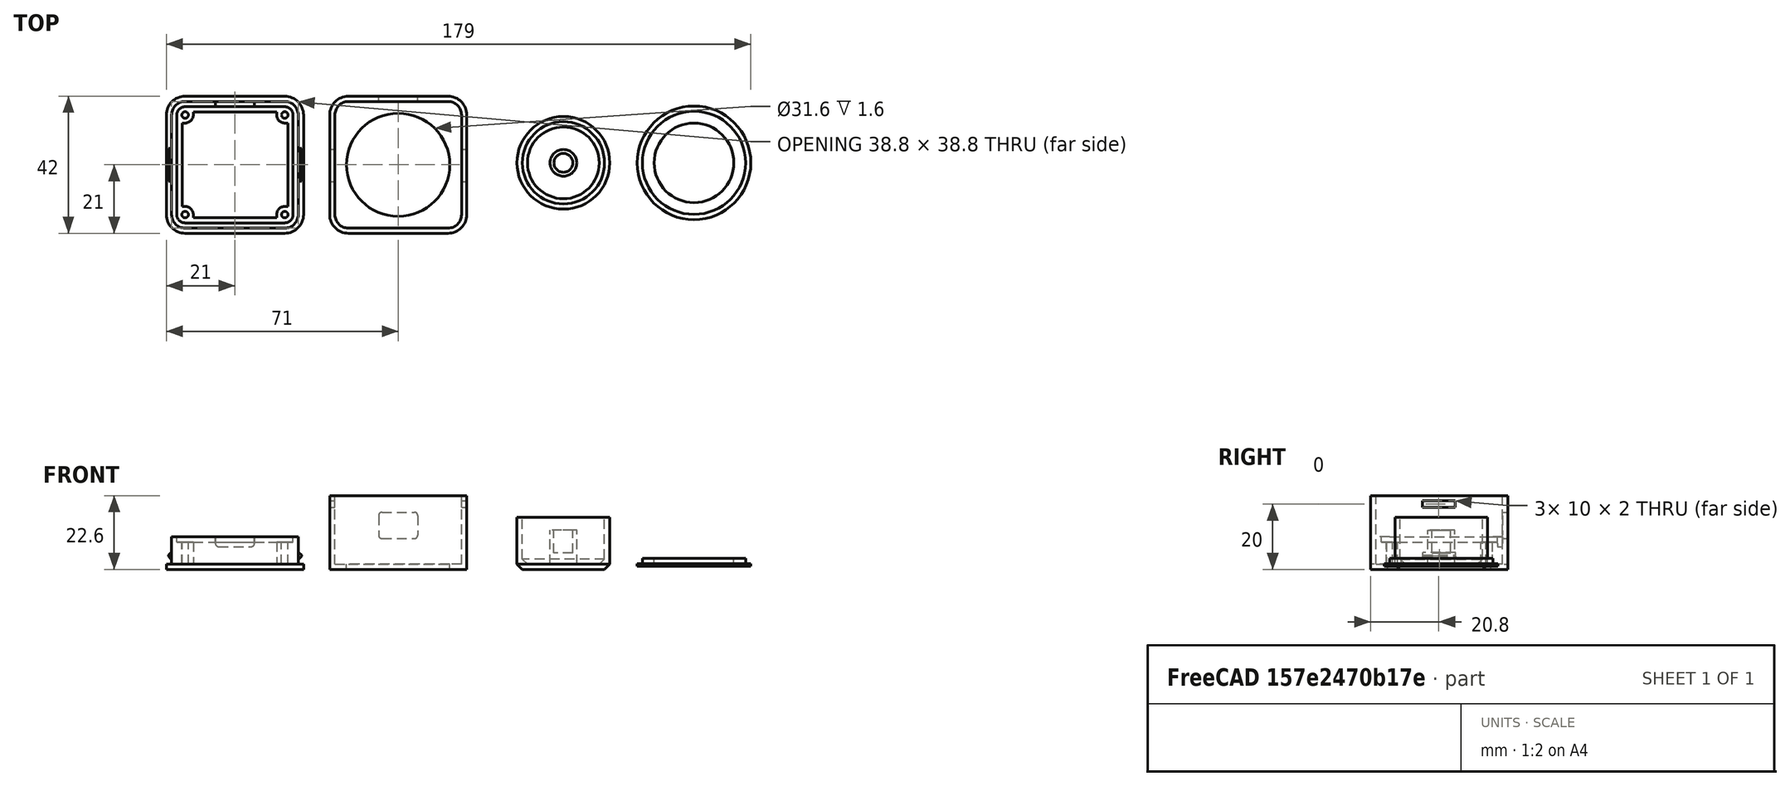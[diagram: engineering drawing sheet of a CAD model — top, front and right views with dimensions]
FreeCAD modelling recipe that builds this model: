
FCSTD DOCUMENT  (FreeCAD 0.19R)
Label: USB_Joystick_case
License: All rights reserved
LicenseURL: http://en.wikipedia.org/wiki/All_rights_reserved
objects: Part::Box×16, Part::Cylinder×12, Part::Fillet×11, Part::Cut×9, Part::MultiFuse×7, Part::Chamfer×4
note: 59 computed .brp shape members not serialized (recipe doc carries the construction recipe); baked Part::Feature solids carry a one-line shape summary decoded from their .brp

FEATURE [Part::Box] Box  label="Boden_aussen"
  AttacherType = Attacher::AttachEngine3D
  Height = 10
  Length = 38.8
  Width = 38.8
FEATURE [Part::Box] Box001  label="Boden_auflage"
  AttacherType = Attacher::AttachEngine3D
  Height = 1.6
  Length = 35.6
  Placement = pos=(1.6,1.6,8.4) rot=(0,0,1;0rad)
  Width = 35.6
FEATURE [Part::Box] Box002  label="Boden_innen"
  AttacherType = Attacher::AttachEngine3D
  Height = 8.4
  Length = 32.4
  Placement = pos=(3.2,3.2,1.6) rot=(0,0,1;0rad)
  Width = 32.4
FEATURE [Part::Cut] Cut
  Base = -> Box
  Tool = -> Box001
FEATURE [Part::Cut] Cut001  label="Boden_grund"
  Base = -> Cut
  Tool = -> Box002
FEATURE [Part::Fillet] Fillet
  Base = -> Cut001
  Edges = 4 edges r=2.54: [Edge17,Edge19,Edge21,Edge22]
FEATURE [Part::Fillet] Fillet001  label="Boden_grund_abgerundet"
  Base = -> Fillet
  Edges = 4 edges r=4.14: [Edge29,Edge30,Edge33,Edge35]
FEATURE [Part::Box] Box003  label="Pfosten_1"
  AttacherType = Attacher::AttachEngine3D
  Height = 8.4
  Length = 5.04
  Placement = pos=(1.6,1.6,0) rot=(0,0,1;0rad)
  Width = 5.04
FEATURE [Part::Cylinder] Cylinder  label="Schraubloch_1"
  Angle = 360
  AttacherType = Attacher::AttachEngine3D
  Height = 6.8
  Placement = pos=(4.14,4.14,1.6) rot=(0,0,1;0rad)
  Radius = 1
FEATURE [Part::Box] Box004  label="Pfosten_002"
  AttacherType = Attacher::AttachEngine3D
  Height = 8.4
  Length = 5.04
  Placement = pos=(32.16,1.6,0) rot=(0,0,1;0rad)
  Width = 5.04
FEATURE [Part::Box] Box005  label="Pfosten_003"
  AttacherType = Attacher::AttachEngine3D
  Height = 8.4
  Length = 5.04
  Placement = pos=(1.6,32.16,0) rot=(0,0,1;0rad)
  Width = 5.04
FEATURE [Part::Box] Box006  label="Pfosten_004"
  AttacherType = Attacher::AttachEngine3D
  Height = 8.4
  Length = 5.04
  Placement = pos=(32.16,32.16,0) rot=(0,0,1;0rad)
  Width = 5.04
FEATURE [Part::Fillet] Fillet002  label="Pfosten_1_abgerundet"
  Base = -> Box003
  Edges = 1 edges r=2.54: [Edge7]
FEATURE [Part::Fillet] Fillet003  label="Pfosten_3_abgerundet"
  Base = -> Box005
  Edges = 1 edges r=2.54: [Edge5]
FEATURE [Part::Fillet] Fillet004  label="Pfosten_4_abgerundet"
  Base = -> Box006
  Edges = 1 edges r=2.54: [Edge1]
FEATURE [Part::Fillet] Fillet005  label="Pfosten_2_abgerundet"
  Base = -> Box004
  Edges = 1 edges r=2.54: [Edge3]
FEATURE [Part::MultiFuse] Fusion  label="Pfosten"
  Shapes = -> [Fillet002,Fillet005,Fillet003,Fillet004]
FEATURE [Part::MultiFuse] Fusion001  label="Boden_mit_pfosten"
  Shapes = -> [Fillet001,Fusion]
FEATURE [Part::Cylinder] Cylinder001  label="Schraubloch_002"
  Angle = 360
  AttacherType = Attacher::AttachEngine3D
  Height = 6.8
  Placement = pos=(34.66,4.14,1.6) rot=(0,0,1;0rad)
  Radius = 1
FEATURE [Part::Cylinder] Cylinder002  label="Schraubloch_003"
  Angle = 360
  AttacherType = Attacher::AttachEngine3D
  Height = 6.8
  Placement = pos=(4.14,34.66,1.6) rot=(0,0,1;0rad)
  Radius = 1
FEATURE [Part::Cylinder] Cylinder003  label="Schraubloch_004"
  Angle = 360
  AttacherType = Attacher::AttachEngine3D
  Height = 6.8
  Placement = pos=(34.66,34.66,1.6) rot=(0,0,1;0rad)
  Radius = 1
FEATURE [Part::MultiFuse] Fusion002  label="Schraublöcher"
  Shapes = -> [Cylinder,Cylinder001,Cylinder002,Cylinder003]
FEATURE [Part::Cut] Cut002  label="Boden_raw"
  Base = -> Fusion001
  Tool = -> Fusion002
FEATURE [Part::Box] Box007  label="Grundplatte"
  AttacherType = Attacher::AttachEngine3D
  Height = 1.6
  Length = 42
  Placement = pos=(-1.6,-1.6,0) rot=(0,0,1;0rad)
  Width = 42
FEATURE [Part::Fillet] Fillet006  label="Bodenplatte_gerundet"
  Base = -> Box007
  Edges = 4 edges r=5.74: [Edge1,Edge3,Edge5,Edge7]
FEATURE [Part::Box] Box008  label="Würfel"
  AttacherType = Attacher::AttachEngine3D
  Height = 8
  Length = 12
  Placement = pos=(13.4,37.2,7) rot=(0,0,1;0rad)
  Width = 10
FEATURE [Part::Fillet] Fillet007  label="USB"
  Base = -> Box008
  Edges = 4 edges r=1: [Edge2,Edge4,Edge6,Edge8]
FEATURE [Part::Box] Box009  label="Würfel001"
  AttacherType = Attacher::AttachEngine3D
  Height = 8
  Length = 12
  Placement = pos=(13.4,37.2,7) rot=(0,0,1;0rad)
  Width = 10
FEATURE [Part::Fillet] Fillet008  label="USB2"
  Base = -> Box009
  Edges = 4 edges r=1: [Edge2,Edge4,Edge6,Edge8]
  Placement = pos=(50,0,2.5) rot=(0,0,1;0rad)
FEATURE [Part::Box] Box010  label="Würfel002"
  AttacherType = Attacher::AttachEngine3D
  Height = 2
  Length = 4
  Placement = pos=(-1,14.4,3.2) rot=(0,0,1;0rad)
  Width = 10
FEATURE [Part::Chamfer] Chamfer  label="Haken1"
  Base = -> Box010
  Edges = 2 edges r=0.8: [Edge2,Edge4]
FEATURE [Part::Box] Box011  label="Würfel003"
  AttacherType = Attacher::AttachEngine3D
  Height = 2
  Length = 1.6
  Placement = pos=(38.2,14.4,3.2) rot=(0,0,1;0rad)
  Width = 10
FEATURE [Part::Chamfer] Chamfer001  label="Haken2"
  Base = -> Box011
  Edges = 2 edges r=0.8: [Edge6,Edge8]
FEATURE [Part::MultiFuse] Fusion003  label="Boden_ohne_USB"
  Shapes = -> [Cut002,Fillet006,Chamfer,Chamfer001]
FEATURE [Part::Cut] Cut003  label="Boden"
  Base = -> Fusion003
  Tool = -> Fillet007
FEATURE [Part::Box] Box012  label="oben_außen"
  AttacherType = Attacher::AttachEngine3D
  Height = 22.6
  Length = 42
  Placement = pos=(48.4,-1.6,0) rot=(0,0,1;0rad)
  Width = 42
FEATURE [Part::Box] Box013  label="oben_innen"
  AttacherType = Attacher::AttachEngine3D
  Height = 21
  Length = 38.8
  Placement = pos=(50,0,1.6) rot=(0,0,1;0rad)
  Width = 38.8
FEATURE [Part::Cylinder] Cylinder004  label="Encoder_loch"
  Angle = 360
  AttacherType = Attacher::AttachEngine3D
  Height = 10
  Placement = pos=(69.4,19.4,0) rot=(0,0,1;0rad)
  Radius = 15.8
FEATURE [Part::Box] Box014  label="Oese1"
  AttacherType = Attacher::AttachEngine3D
  Height = 2
  Length = 10.4
  Placement = pos=(46,14.2,19) rot=(0,0,1;0rad)
  Width = 10
FEATURE [Part::Box] Box015  label="Oese2"
  AttacherType = Attacher::AttachEngine3D
  Height = 2
  Length = 10.4
  Placement = pos=(83,14.2,19) rot=(0,0,1;0rad)
  Width = 10
FEATURE [Part::MultiFuse] Fusion004  label="Deckel_aussparungen"
  Shapes = -> [Fillet008,Cylinder004,Box014,Box015]
FEATURE [Part::Cylinder] Cylinder005  label="grund_außen"
  Angle = 360
  AttacherType = Attacher::AttachEngine3D
  Height = 16
  Placement = pos=(120,20,0) rot=(0,0,1;0rad)
  Radius = 14.2
FEATURE [Part::Cylinder] Cylinder006  label="grund_innen"
  Angle = 360
  AttacherType = Attacher::AttachEngine3D
  Height = 14.4
  Placement = pos=(120,20,1.6) rot=(0,0,1;0rad)
  Radius = 12.6
FEATURE [Part::Cut] Cut006  label="basis_roh"
  Base = -> Cylinder005
  Tool = -> Cylinder006
FEATURE [Part::Chamfer] Chamfer002
  Base = -> Cut006
  Edges = 1 edges r=1.6: [Edge6]
FEATURE [Part::Chamfer] Chamfer003  label="Basis"
  Base = -> Chamfer002
  Edges = 1 edges r=1.6: [Edge8]
FEATURE [Part::Cylinder] Cylinder007  label="shaft_außen"
  Angle = 360
  AttacherType = Attacher::AttachEngine3D
  Height = 12
  Placement = pos=(120,20,0) rot=(0,0,1;0rad)
  Radius = 4.1
FEATURE [Part::Cylinder] Cylinder008  label="shaft_innen"
  Angle = 360
  AttacherType = Attacher::AttachEngine3D
  Height = 7
  Placement = pos=(120,20,5) rot=(0,0,1;0rad)
  Radius = 2.9
FEATURE [Part::Cut] Cut007  label="Shaft"
  Base = -> Cylinder007
  Tool = -> Cylinder008
FEATURE [Part::Cylinder] Cylinder009  label="LED_ring_big"
  Angle = 360
  AttacherType = Attacher::AttachEngine3D
  Height = 0.8
  Placement = pos=(160,20,1) rot=(0,0,1;0rad)
  Radius = 17.4
FEATURE [Part::Cylinder] Cylinder010  label="LED_ring_small"
  Angle = 360
  AttacherType = Attacher::AttachEngine3D
  Height = 2.4
  Placement = pos=(160,20,1) rot=(0,0,1;0rad)
  Radius = 15.8
FEATURE [Part::MultiFuse] Fusion006  label="LED_Ring_roh"
  Shapes = -> [Cylinder009,Cylinder010]
FEATURE [Part::Cylinder] Cylinder011  label="LED_ring_hole"
  Angle = 360
  AttacherType = Attacher::AttachEngine3D
  Height = 2.4
  Placement = pos=(160,20,1) rot=(0,0,1;0rad)
  Radius = 12.2
FEATURE [Part::Cut] Cut008  label="LED-Ring"
  Base = -> Fusion006
  Tool = -> Cylinder011
FEATURE [Part::MultiFuse] Fusion005  label="Knob"
  Shapes = -> [Chamfer003,Cut007]
FEATURE [Part::Cut] Cut009  label="Top_raw"
  Base = -> Box012
  Tool = -> Box013
FEATURE [Part::Fillet] Fillet009
  Base = -> Cut009
  Edges = 4 edges r=4.14: [Edge17,Edge18,Edge21,Edge22]
FEATURE [Part::Fillet] Fillet010  label="Deckel_gerundet"
  Base = -> Fillet009
  Edges = 4 edges r=5.74: [Edge29,Edge30,Edge33,Edge35]
FEATURE [Part::Cut] Cut010  label="Deckel"
  Base = -> Fillet010
  Tool = -> Fusion004
